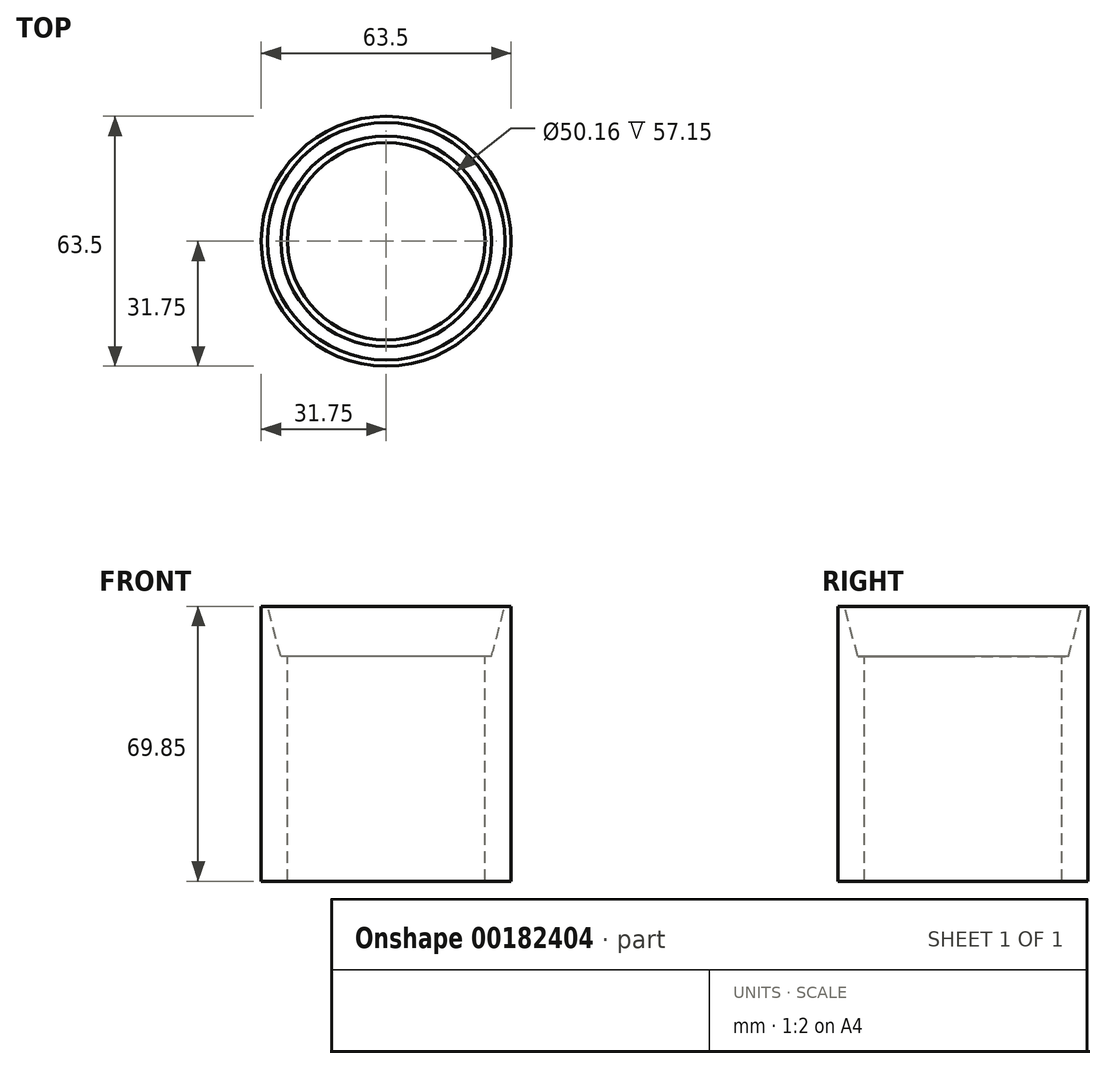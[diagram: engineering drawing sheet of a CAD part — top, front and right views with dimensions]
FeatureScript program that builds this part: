
annotation { "Feature Type Name" : "Feature", "Feature Type Description" : "" }
export const myFeature = defineFeature(function(context is Context, id is Id, definition is map)
    precondition{}
    {
        {
            var Q0;
            Q0=qCreatedBy(makeId("Top.planeOp"),FACE);
            var sketch = newSketch(context, id + "F0", { "sketchPlane" : qUnion([Q0])});
            skCircle(sketch, "E0", {"center": v(0, 0) * mm, "radius": 31.75 * mm});
            skSolve(sketch);
        }
        {
            var Q0;
            Q0 = qSketchRegion(id + "F0", true);
            extrude(context, id + "F1", {"entities" : qUnion([Q0]), "depth" : 69.85 * mm});
        }
        {
            var Q0;
            Q0=makeQuery(id+"F1.opExtrude","CAP_FACE",FACE,{"disambiguationData":[OSD([sQuery(id+"F0.wireOp",EDGE,"E0")])],"isStart":false});
            var sketch = newSketch(context, id + "F2", { "sketchPlane" : qUnion([Q0])});
            skCircle(sketch, "E1", {"center": v(0, 0) * mm, "radius": 30.16 * mm});
            skSolve(sketch);
        }
        {
            var Q0;
            Q0 = qSketchRegion(id + "F2", true);
            extrude(context, id + "F3", {"entities" : qUnion([Q0]), "operationType" : NewBodyOperationType.REMOVE, "oppositeDirection" : true, "depth" : 12.7 * mm, "hasDraft" : true, "draftAngle" : 15 * degree, "draftPullDirection" : true});
        }
        {
            var Q0;
            Q0=makeQuery(id+"F3.boolean.opBoolean","COPY",FACE,{"derivedFrom":makeQuery(id+"F3.opExtrude","CAP_FACE",FACE,{"disambiguationData":[OSD([sQuery(id+"F2.wireOp",EDGE,"E1")])],"isStart":false})});
            var sketch = newSketch(context, id + "F4", { "sketchPlane" : qUnion([Q0])});
            skCircle(sketch, "E2", {"center": v(0, 0) * mm, "radius": 25.08 * mm});
            skSolve(sketch);
        }
        {
            var Q0;
            Q0 = qSketchRegion(id + "F4", true);
            extrude(context, id + "F5", {"entities" : qUnion([Q0]), "operationType" : NewBodyOperationType.REMOVE, "endBound" : BoundingType.THROUGH_ALL, "oppositeDirection" : true, "depth" : 25.4 * mm});
        }
    });
